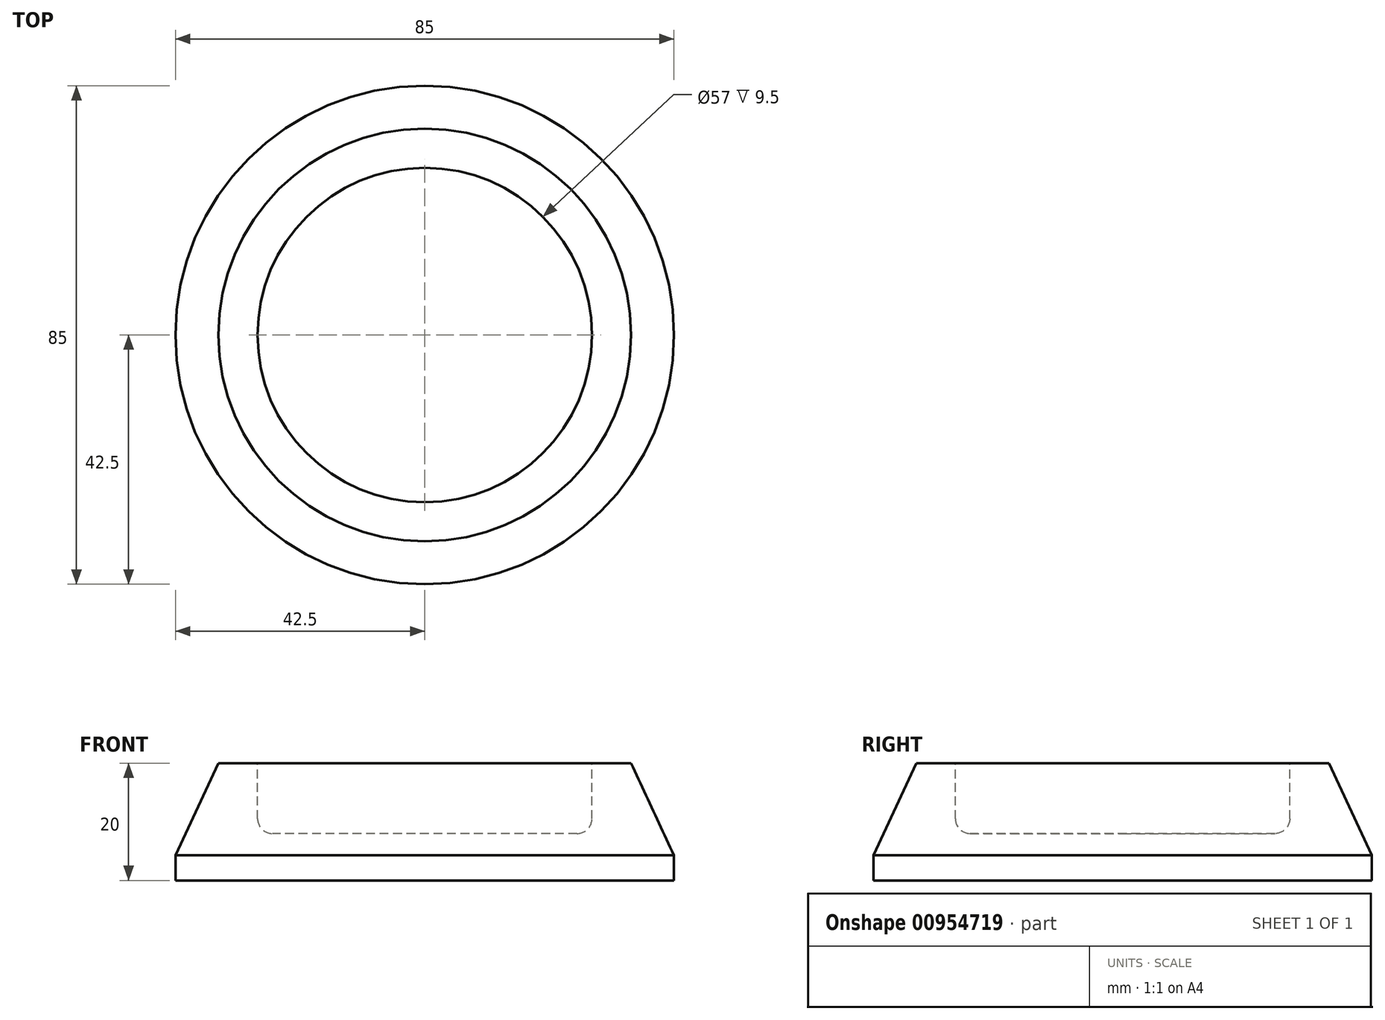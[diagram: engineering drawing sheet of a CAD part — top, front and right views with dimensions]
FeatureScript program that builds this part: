
annotation { "Feature Type Name" : "Feature", "Feature Type Description" : "" }
export const myFeature = defineFeature(function(context is Context, id is Id, definition is map)
    precondition{}
    {
        {
            var Q0;
            Q0=qCreatedBy(makeId("Top.planeOp"),FACE);
            var sketch = newSketch(context, id + "F0", { "sketchPlane" : qUnion([Q0])});
            skCircle(sketch, "E0", {"center": v(0, 0) * mm, "radius": 44.5 * mm});
            skSolve(sketch);
        }
        {
            var Q0;
            Q0 = qSketchRegion(id + "F0", true);
            extrude(context, id + "F1", {"entities" : qUnion([Q0]), "depth" : 20 * mm, "offsetDistance" : 25 * mm, "hasDraft" : true, "draftAngle" : 25 * degree, "draftPullDirection" : true});
        }
        {
            var Q0;
            Q0=makeQuery(id+"F1.opExtrude","CAP_FACE",FACE,{"disambiguationData":[OSD([sQuery(id+"F0.wireOp",EDGE,"E0")])],"isStart":false});
            var sketch = newSketch(context, id + "F2", { "sketchPlane" : qUnion([Q0])});
            skCircle(sketch, "E1", {"center": v(0, 0) * mm, "radius": 28.5 * mm});
            skSolve(sketch);
        }
        {
            var Q0;
            Q0 = qSketchRegion(id + "F2", true);
            extrude(context, id + "F3", {"entities" : qUnion([Q0]), "operationType" : NewBodyOperationType.REMOVE, "oppositeDirection" : true, "depth" : 12 * mm, "offsetDistance" : 25 * mm});
        }
        {
            var Q0;
            {var subQ0=makeQuery(id+"F8Lvc3j9PHc0zEE_1.boolean.opBoolean","MERGE",FACE,{"derivedFrom":[makeQuery(id+"F1.opExtrude","CAP_FACE",FACE,{"disambiguationData":[OSD([sQuery(id+"F0.wireOp",EDGE,"E0")])],"isStart":true}),makeQuery(id+"F8Lvc3j9PHc0zEE_1.opExtrude","CAP_FACE",FACE,{"disambiguationData":[OSD([sQuery(id+"FwLqoiMPC6SEHfm_1.wireOp",EDGE,"GycJxp22-FZYK-1OxP-QzMf-KDCXq2wEEyBk.top"),sQuery(id+"FwLqoiMPC6SEHfm_1.wireOp",EDGE,"GycJxp22-FZYK-1OxP-QzMf-KDCXq2wEEyBk.left"),sQuery(id+"FwLqoiMPC6SEHfm_1.wireOp",EDGE,"GycJxp22-FZYK-1OxP-QzMf-KDCXq2wEEyBk.right"),sQuery(id+"FwLqoiMPC6SEHfm_1.wireOp",EDGE,"CL3XvOeo-Ak8D-gTUA-dsL4-e7HWhR4VhFDQ"),sQuery(id+"FwLqoiMPC6SEHfm_1.wireOp",EDGE,"8vuTaFH0-ThpJ-Fc5W-8Fak-dPNbpc9N16ZV")])],"isStart":true})]});Q0=makeQuery(id+"FOQ7FE29LTqZ2ab_1.opBoolean","MERGE",FACE,{"derivedFrom":[subQ0,makeQuery(id+"F5Tso9rccu1SIYW_1.opPattern","COPY",FACE,{"derivedFrom":subQ0,"instanceName":"1"}),makeQuery(id+"F5Tso9rccu1SIYW_1.opPattern","COPY",FACE,{"derivedFrom":subQ0,"instanceName":"2"}),makeQuery(id+"F5Tso9rccu1SIYW_1.opPattern","COPY",FACE,{"derivedFrom":subQ0,"instanceName":"3"}),makeQuery(id+"F5Tso9rccu1SIYW_1.opPattern","COPY",FACE,{"derivedFrom":subQ0,"instanceName":"4"}),makeQuery(id+"F5Tso9rccu1SIYW_1.opPattern","COPY",FACE,{"derivedFrom":subQ0,"instanceName":"5"}),makeQuery(id+"F5Tso9rccu1SIYW_1.opPattern","COPY",FACE,{"derivedFrom":subQ0,"instanceName":"6"}),makeQuery(id+"F5Tso9rccu1SIYW_1.opPattern","COPY",FACE,{"derivedFrom":subQ0,"instanceName":"7"})]});}
            var sketch = newSketch(context, id + "F4", { "sketchPlane" : qUnion([Q0])});
            skCircle(sketch, "E2", {"center": v(0, 0) * mm, "radius": 42.5 * mm});
            skCircle(sketch, "E3.0", {"center": v(0, 0) * mm, "radius": 44.5 * mm});
            skSolve(sketch);
        }
        {
            var Q0;
            Q0 = qSketchRegion(id + "F4", true);
            extrude(context, id + "F5", {"entities" : qUnion([Q0]), "operationType" : NewBodyOperationType.REMOVE, "endBound" : BoundingType.THROUGH_ALL, "oppositeDirection" : true, "depth" : 25 * mm, "offsetDistance" : 25 * mm});
        }
        {
            var Q0;
            Q0=makeQuery(id+"F3.boolean.opBoolean","COPY",FACE,{"derivedFrom":makeQuery(id+"F3.opExtrude","CAP_FACE",FACE,{"disambiguationData":[OSD([sQuery(id+"F2.wireOp",EDGE,"E1")])],"isStart":false})});
            fillet(context, id + "F6", {"entities" : qUnion([Q0]), "radius" : 2.5 * mm, "tangentPropagation" : true, "allowEdgeOverflow" : false});
        }
    });
